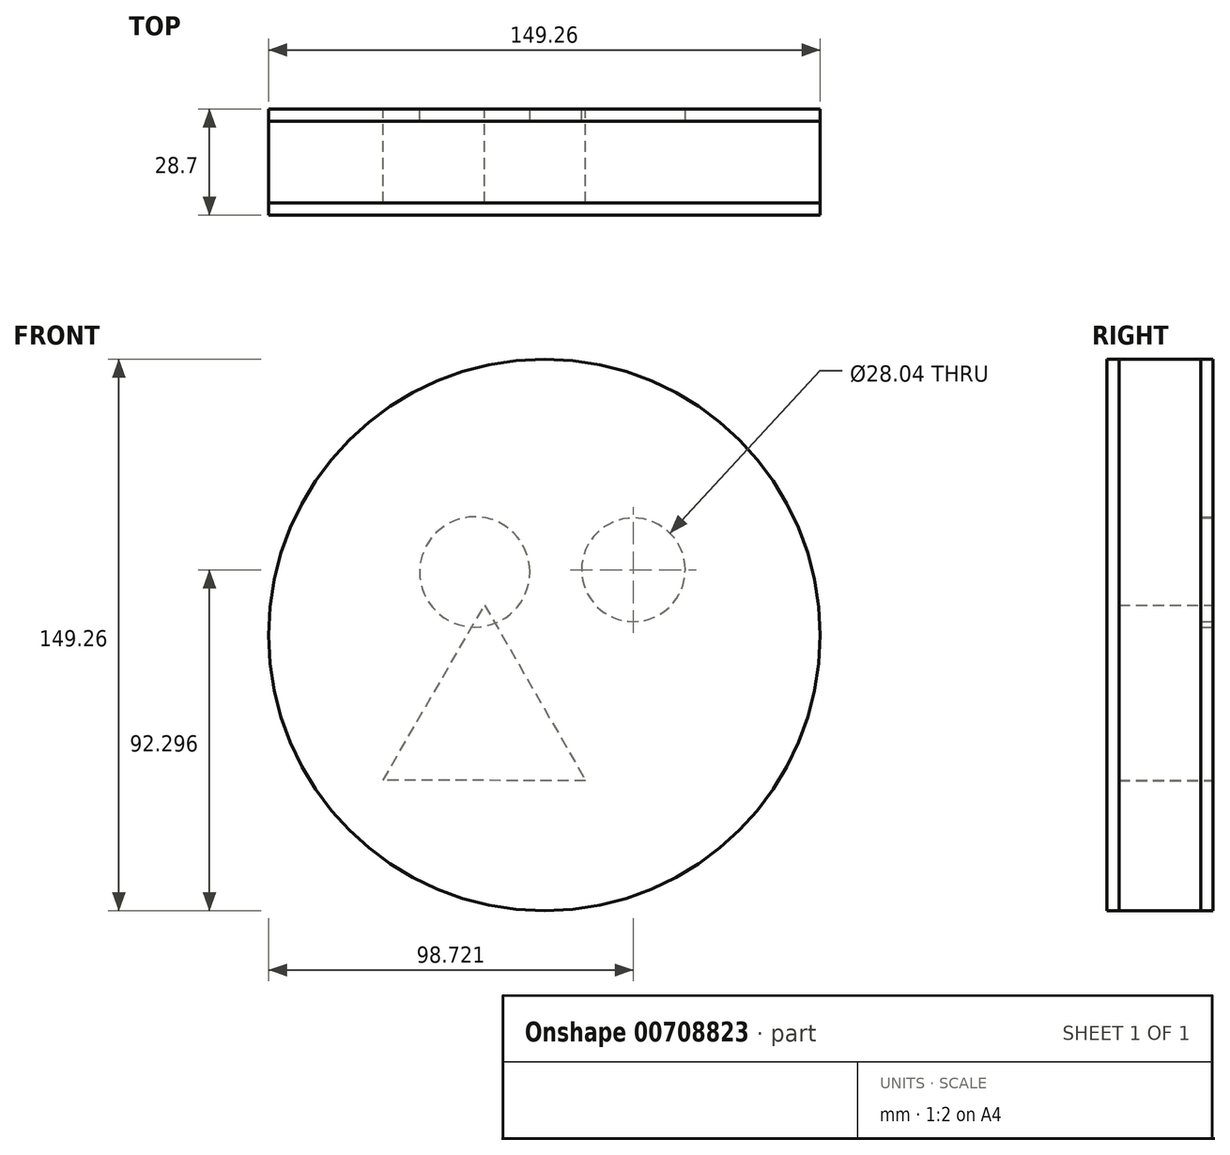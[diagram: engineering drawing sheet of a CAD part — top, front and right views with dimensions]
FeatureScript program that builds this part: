
annotation { "Feature Type Name" : "Feature", "Feature Type Description" : "" }
export const myFeature = defineFeature(function(context is Context, id is Id, definition is map)
    precondition{}
    {
        {
            var Q0;
            Q0=qCreatedBy(makeId("Front.planeOp"),FACE);
            var sketch = newSketch(context, id + "F0", { "sketchPlane" : qUnion([Q0])});
            skCircle(sketch, "E0", {"center": v(0, 0) * mm, "radius": 74.63 * mm});
            skSolve(sketch);
        }
        {
            var Q0;
            Q0=makeQuery(id+"F0.imprint","IMPRINT",FACE,{"disambiguationData":[TD([[makeQuery(id+"F0.imprint","IMPRINT",EDGE,{"derivedFrom":sQuery(id+"F0.wireOp",EDGE,"E0")}),1.0]])]});
            var sketch = newSketch(context, id + "F1", { "sketchPlane" : qUnion([Q0])});
            skCircle(sketch, "E1", {"center": v(-18.83, 17.08) * mm, "radius": 14.9 * mm});
            skSolve(sketch);
        }
        {
            var Q0;
            Q0=makeQuery(id+"F0.imprint","IMPRINT",FACE,{"disambiguationData":[TD([[makeQuery(id+"F0.imprint","IMPRINT",EDGE,{"derivedFrom":sQuery(id+"F0.wireOp",EDGE,"E0")}),1.0]])]});
            var sketch = newSketch(context, id + "F2", { "sketchPlane" : qUnion([Q0])});
            skCircle(sketch, "E2", {"center": v(24.1, 17.67) * mm, "radius": 14.02 * mm});
            skSolve(sketch);
        }
        {
            var Q0;
            Q0=makeQuery(id+"F0.imprint","IMPRINT",FACE,{"disambiguationData":[TD([[makeQuery(id+"F0.imprint","IMPRINT",EDGE,{"derivedFrom":sQuery(id+"F0.wireOp",EDGE,"E0")}),1.0]])]});
            var sketch = newSketch(context, id + "F3", { "sketchPlane" : qUnion([Q0])});
            skCircle(sketch, "E3.cCircle", {"center": v(-16.2, -23.5) * mm, "radius": 15.83 * mm, "construction": true});
            skLineSegment(sketch, "E3.0", {"start": v(-16.14, 8.15) * mm, "end": v(11.17, -39.4) * mm});
            skLineSegment(sketch, "E3.1", {"start": v(11.17, -39.4) * mm, "end": v(-43.66, -39.27) * mm});
            skLineSegment(sketch, "E3.2", {"start": v(-43.66, -39.27) * mm, "end": v(-16.14, 8.15) * mm});
            skPoint(sketch, "E3.0.midPoint", {"position": v(-2.48, -15.62) * mm});
            skSolve(sketch);
        }
        {
            var Q0;
            Q0 = qSketchRegion(id + "F3", true);
            var Q1;
            Q1=makeQuery(id+"F0.imprint","IMPRINT",FACE,{"disambiguationData":[TD([[makeQuery(id+"F0.imprint","IMPRINT",EDGE,{"derivedFrom":sQuery(id+"F0.wireOp",EDGE,"E0")}),1.0]])]});
            extrude(context, id + "F4", {"entities" : qUnion([Q0, Q1]), "depth" : 25.4 * mm, "offsetDistance" : 25.4 * mm});
        }
        {
            var Q0;
            Q0=makeQuery(id+"F4.opExtrude","CAP_FACE",FACE,{"disambiguationData":[OSD([sQuery(id+"F0.wireOp",EDGE,"E0")])],"isStart":false});
            var Q1;
            Q1=makeQuery(id+"F2.imprint","IMPRINT",FACE,{"disambiguationData":[TD([[makeQuery(id+"F2.imprint","IMPRINT",EDGE,{"derivedFrom":sQuery(id+"F2.wireOp",EDGE,"E2")}),-1.0]])]});
            var Q2;
            Q2=makeQuery(id+"F1.imprint","IMPRINT",FACE,{"disambiguationData":[TD([[makeQuery(id+"F1.imprint","IMPRINT",EDGE,{"derivedFrom":sQuery(id+"F1.wireOp",EDGE,"E1")}),1.0]])]});
            extrude(context, id + "F5", {"entities" : qUnion([Q0, Q1, Q2]), "depth" : 3.3 * mm, "offsetDistance" : 25.4 * mm});
        }
    });
